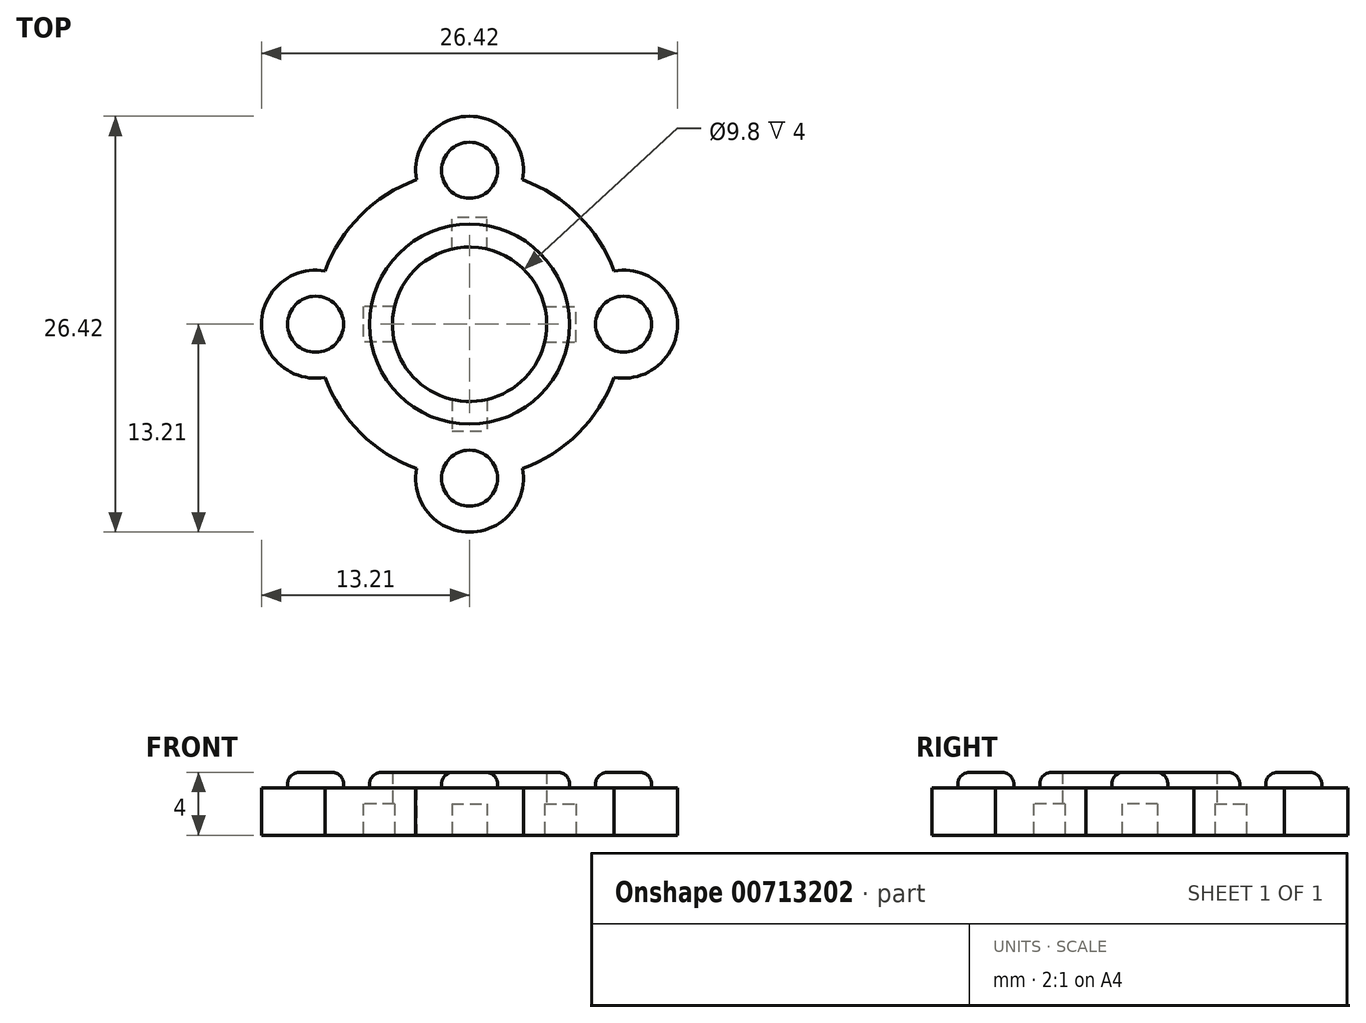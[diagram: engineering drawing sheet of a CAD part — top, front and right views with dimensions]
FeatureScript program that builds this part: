
annotation { "Feature Type Name" : "Feature", "Feature Type Description" : "" }
export const myFeature = defineFeature(function(context is Context, id is Id, definition is map)
    precondition{}
    {
        {
            var Q0;
            Q0=qCreatedBy(makeId("Top.planeOp"),FACE);
            var sketch = newSketch(context, id + "F0", { "sketchPlane" : qUnion([Q0])});
            skCircle(sketch, "E0", {"center": v(0, 0) * mm, "radius": 6.35 * mm});
            skCircle(sketch, "E1", {"center": v(0, 0) * mm, "radius": 9.78 * mm});
            skCircle(sketch, "E2", {"center": v(0, 9.78) * mm, "radius": 1.78 * mm});
            skCircle(sketch, "E3", {"center": v(0, 9.78) * mm, "radius": 3.43 * mm});
            skCircle(sketch, "E4.1.0", {"center": v(-9.78, 0) * mm, "radius": 3.43 * mm});
            skCircle(sketch, "E4.1.1", {"center": v(-9.78, 0) * mm, "radius": 1.78 * mm});
            skCircle(sketch, "E4.2.0", {"center": v(0, -9.78) * mm, "radius": 3.43 * mm});
            skCircle(sketch, "E4.2.1", {"center": v(0, -9.78) * mm, "radius": 1.78 * mm});
            skCircle(sketch, "E4.3.0", {"center": v(9.78, 0) * mm, "radius": 3.43 * mm});
            skCircle(sketch, "E4.3.1", {"center": v(9.78, 0) * mm, "radius": 1.78 * mm});
            skCircle(sketch, "E5", {"center": v(0, 0) * mm, "radius": 4.9 * mm});
            skSolve(sketch);
        }
        {
            var Q0;
            {var subQ0=sQuery(id+"F0.wireOp",EDGE,"E4.1.1");var subQ1=sQuery(id+"F0.wireOp",EDGE,"E1");var subQ2=makeQuery(id+"F0.imprint","INTERSECT",VERTEX,{"disambiguationData":[OD(0.0)],"derivedFrom":[subQ1,subQ0]});Q0=makeQuery(id+"F0.imprint","IMPRINT",FACE,{"disambiguationData":[TD([[makeQuery(id+"F0.imprint","IMPRINT",EDGE,{"disambiguationData":[TD([[subQ2,-1.0]])],"derivedFrom":subQ1}),-1.0]])]});}
            var Q1;
            {var subQ0=sQuery(id+"F0.wireOp",EDGE,"E2");var subQ1=sQuery(id+"F0.wireOp",EDGE,"E1");var subQ2=makeQuery(id+"F0.imprint","INTERSECT",VERTEX,{"disambiguationData":[OD(0.0)],"derivedFrom":[subQ1,subQ0]});Q1=makeQuery(id+"F0.imprint","IMPRINT",FACE,{"disambiguationData":[TD([[makeQuery(id+"F0.imprint","IMPRINT",EDGE,{"disambiguationData":[TD([[subQ2,-1.0]])],"derivedFrom":subQ1}),-1.0]])]});}
            var Q2;
            {var subQ0=sQuery(id+"F0.wireOp",EDGE,"E4.1.0");var subQ1=sQuery(id+"F0.wireOp",EDGE,"E0");var subQ2=makeQuery(id+"F0.imprint","INTERSECT",VERTEX,{"derivedFrom":[subQ1,subQ0]});Q2=makeQuery(id+"F0.imprint","IMPRINT",FACE,{"disambiguationData":[TD([[makeQuery(id+"F0.imprint","IMPRINT",EDGE,{"disambiguationData":[TD([[subQ2,-1.0]])],"derivedFrom":subQ1}),-1.0]])]});}
            var Q3;
            {var subQ0=sQuery(id+"F0.wireOp",EDGE,"E4.1.1");var subQ1=sQuery(id+"F0.wireOp",EDGE,"E1");var subQ2=makeQuery(id+"F0.imprint","INTERSECT",VERTEX,{"disambiguationData":[OD(0.0)],"derivedFrom":[subQ1,subQ0]});Q3=makeQuery(id+"F0.imprint","IMPRINT",FACE,{"disambiguationData":[TD([[makeQuery(id+"F0.imprint","IMPRINT",EDGE,{"disambiguationData":[TD([[subQ2,-1.0]])],"derivedFrom":subQ1}),1.0]])]});}
            var Q4;
            {var subQ0=sQuery(id+"F0.wireOp",EDGE,"E4.2.0");var subQ1=sQuery(id+"F0.wireOp",EDGE,"E1");var subQ4=makeQuery(id+"F0.imprint","INTERSECT",VERTEX,{"disambiguationData":[OD(0.0)],"derivedFrom":[subQ1,subQ0]});Q4=makeQuery(id+"F0.imprint","IMPRINT",FACE,{"disambiguationData":[TD([[makeQuery(id+"F0.imprint","IMPRINT",EDGE,{"disambiguationData":[TD([[subQ4,-1.0]])],"derivedFrom":subQ1}),1.0]])]});}
            var Q5;
            {var subQ0=sQuery(id+"F0.wireOp",EDGE,"E4.3.0");var subQ1=sQuery(id+"F0.wireOp",EDGE,"E1");var subQ4=makeQuery(id+"F0.imprint","INTERSECT",VERTEX,{"disambiguationData":[OD(0.0)],"derivedFrom":[subQ1,subQ0]});Q5=makeQuery(id+"F0.imprint","IMPRINT",FACE,{"disambiguationData":[TD([[makeQuery(id+"F0.imprint","IMPRINT",EDGE,{"disambiguationData":[TD([[subQ4,1.0]])],"derivedFrom":subQ1}),1.0]])]});}
            var Q6;
            {var subQ0=sQuery(id+"F0.wireOp",EDGE,"E4.1.0");var subQ1=sQuery(id+"F0.wireOp",EDGE,"E1");var subQ2=makeQuery(id+"F0.imprint","INTERSECT",VERTEX,{"disambiguationData":[OD(0.0)],"derivedFrom":[subQ1,subQ0]});Q6=makeQuery(id+"F0.imprint","IMPRINT",FACE,{"disambiguationData":[TD([[makeQuery(id+"F0.imprint","IMPRINT",EDGE,{"disambiguationData":[TD([[subQ2,-1.0]])],"derivedFrom":subQ1}),1.0]])]});}
            var Q7;
            {var subQ0=sQuery(id+"F0.wireOp",EDGE,"E4.3.1");var subQ1=sQuery(id+"F0.wireOp",EDGE,"E1");var subQ2=makeQuery(id+"F0.imprint","INTERSECT",VERTEX,{"disambiguationData":[OD(0.0)],"derivedFrom":[subQ1,subQ0]});Q7=makeQuery(id+"F0.imprint","IMPRINT",FACE,{"disambiguationData":[TD([[makeQuery(id+"F0.imprint","IMPRINT",EDGE,{"disambiguationData":[TD([[subQ2,1.0]])],"derivedFrom":subQ1}),-1.0]])]});}
            var Q8;
            {var subQ0=sQuery(id+"F0.wireOp",EDGE,"E4.2.1");var subQ1=sQuery(id+"F0.wireOp",EDGE,"E1");var subQ2=makeQuery(id+"F0.imprint","INTERSECT",VERTEX,{"disambiguationData":[OD(0.0)],"derivedFrom":[subQ1,subQ0]});Q8=makeQuery(id+"F0.imprint","IMPRINT",FACE,{"disambiguationData":[TD([[makeQuery(id+"F0.imprint","IMPRINT",EDGE,{"disambiguationData":[TD([[subQ2,-1.0]])],"derivedFrom":subQ1}),-1.0]])]});}
            var Q9;
            {var subQ0=sQuery(id+"F0.wireOp",EDGE,"E4.1.0");var subQ1=sQuery(id+"F0.wireOp",EDGE,"E1");var subQ2=makeQuery(id+"F0.imprint","INTERSECT",VERTEX,{"disambiguationData":[OD(0.0)],"derivedFrom":[subQ1,subQ0]});Q9=makeQuery(id+"F0.imprint","IMPRINT",FACE,{"disambiguationData":[TD([[makeQuery(id+"F0.imprint","IMPRINT",EDGE,{"disambiguationData":[TD([[subQ2,-1.0]])],"derivedFrom":subQ1}),-1.0]])]});}
            var Q10;
            {var subQ0=sQuery(id+"F0.wireOp",EDGE,"E2");var subQ1=sQuery(id+"F0.wireOp",EDGE,"E1");var subQ2=makeQuery(id+"F0.imprint","INTERSECT",VERTEX,{"disambiguationData":[OD(0.0)],"derivedFrom":[subQ1,subQ0]});Q10=makeQuery(id+"F0.imprint","IMPRINT",FACE,{"disambiguationData":[TD([[makeQuery(id+"F0.imprint","IMPRINT",EDGE,{"disambiguationData":[TD([[subQ2,-1.0]])],"derivedFrom":subQ1}),1.0]])]});}
            var Q11;
            {var subQ0=sQuery(id+"F0.wireOp",EDGE,"E3");var subQ1=sQuery(id+"F0.wireOp",EDGE,"E1");var subQ2=makeQuery(id+"F0.imprint","INTERSECT",VERTEX,{"disambiguationData":[OD(0.0)],"derivedFrom":[subQ1,subQ0]});Q11=makeQuery(id+"F0.imprint","IMPRINT",FACE,{"disambiguationData":[TD([[makeQuery(id+"F0.imprint","IMPRINT",EDGE,{"disambiguationData":[TD([[subQ2,-1.0]])],"derivedFrom":subQ1}),-1.0]])]});}
            var Q12;
            {var subQ0=sQuery(id+"F0.wireOp",EDGE,"E4.3.0");var subQ1=sQuery(id+"F0.wireOp",EDGE,"E1");var subQ2=makeQuery(id+"F0.imprint","INTERSECT",VERTEX,{"disambiguationData":[OD(0.0)],"derivedFrom":[subQ1,subQ0]});Q12=makeQuery(id+"F0.imprint","IMPRINT",FACE,{"disambiguationData":[TD([[makeQuery(id+"F0.imprint","IMPRINT",EDGE,{"disambiguationData":[TD([[subQ2,1.0]])],"derivedFrom":subQ1}),-1.0]])]});}
            var Q13;
            Q13=makeQuery(id+"F0.imprint","IMPRINT",FACE,{"disambiguationData":[TD([[makeQuery(id+"F0.imprint","IMPRINT",EDGE,{"derivedFrom":sQuery(id+"F0.wireOp",EDGE,"E5")}),-1.0]])]});
            var Q14;
            {var subQ0=sQuery(id+"F0.wireOp",EDGE,"E3");var subQ1=sQuery(id+"F0.wireOp",EDGE,"E0");var subQ2=makeQuery(id+"F0.imprint","INTERSECT",VERTEX,{"derivedFrom":[subQ1,subQ0]});Q14=makeQuery(id+"F0.imprint","IMPRINT",FACE,{"disambiguationData":[TD([[makeQuery(id+"F0.imprint","IMPRINT",EDGE,{"disambiguationData":[TD([[subQ2,-1.0]])],"derivedFrom":subQ1}),-1.0]])]});}
            var Q15;
            {var subQ0=sQuery(id+"F0.wireOp",EDGE,"E4.3.0");var subQ1=sQuery(id+"F0.wireOp",EDGE,"E0");var subQ2=makeQuery(id+"F0.imprint","INTERSECT",VERTEX,{"derivedFrom":[subQ1,subQ0]});Q15=makeQuery(id+"F0.imprint","IMPRINT",FACE,{"disambiguationData":[TD([[makeQuery(id+"F0.imprint","IMPRINT",EDGE,{"disambiguationData":[TD([[subQ2,1.0]])],"derivedFrom":subQ1}),-1.0]])]});}
            var Q16;
            {var subQ0=sQuery(id+"F0.wireOp",EDGE,"E3");var subQ1=sQuery(id+"F0.wireOp",EDGE,"E0");var subQ2=makeQuery(id+"F0.imprint","INTERSECT",VERTEX,{"derivedFrom":[subQ1,subQ0]});Q16=makeQuery(id+"F0.imprint","IMPRINT",FACE,{"disambiguationData":[TD([[makeQuery(id+"F0.imprint","IMPRINT",EDGE,{"disambiguationData":[TD([[subQ2,1.0]])],"derivedFrom":subQ1}),-1.0]])]});}
            var Q17;
            {var subQ0=sQuery(id+"F0.wireOp",EDGE,"E4.3.1");var subQ1=sQuery(id+"F0.wireOp",EDGE,"E1");var subQ2=makeQuery(id+"F0.imprint","INTERSECT",VERTEX,{"disambiguationData":[OD(0.0)],"derivedFrom":[subQ1,subQ0]});Q17=makeQuery(id+"F0.imprint","IMPRINT",FACE,{"disambiguationData":[TD([[makeQuery(id+"F0.imprint","IMPRINT",EDGE,{"disambiguationData":[TD([[subQ2,1.0]])],"derivedFrom":subQ1}),1.0]])]});}
            var Q18;
            {var subQ0=sQuery(id+"F0.wireOp",EDGE,"E4.2.1");var subQ1=sQuery(id+"F0.wireOp",EDGE,"E1");var subQ2=makeQuery(id+"F0.imprint","INTERSECT",VERTEX,{"disambiguationData":[OD(0.0)],"derivedFrom":[subQ1,subQ0]});Q18=makeQuery(id+"F0.imprint","IMPRINT",FACE,{"disambiguationData":[TD([[makeQuery(id+"F0.imprint","IMPRINT",EDGE,{"disambiguationData":[TD([[subQ2,-1.0]])],"derivedFrom":subQ1}),1.0]])]});}
            var Q19;
            {var subQ0=sQuery(id+"F0.wireOp",EDGE,"E3");var subQ1=sQuery(id+"F0.wireOp",EDGE,"E1");var subQ7=makeQuery(id+"F0.imprint","INTERSECT",VERTEX,{"disambiguationData":[OD(0.0)],"derivedFrom":[subQ1,subQ0]});Q19=makeQuery(id+"F0.imprint","IMPRINT",FACE,{"disambiguationData":[TD([[makeQuery(id+"F0.imprint","IMPRINT",EDGE,{"disambiguationData":[TD([[subQ7,-1.0]])],"derivedFrom":subQ1}),1.0]])]});}
            var Q20;
            {var subQ0=sQuery(id+"F0.wireOp",EDGE,"E4.2.0");var subQ1=sQuery(id+"F0.wireOp",EDGE,"E1");var subQ2=makeQuery(id+"F0.imprint","INTERSECT",VERTEX,{"disambiguationData":[OD(0.0)],"derivedFrom":[subQ1,subQ0]});Q20=makeQuery(id+"F0.imprint","IMPRINT",FACE,{"disambiguationData":[TD([[makeQuery(id+"F0.imprint","IMPRINT",EDGE,{"disambiguationData":[TD([[subQ2,-1.0]])],"derivedFrom":subQ1}),-1.0]])]});}
            extrude(context, id + "F1", {"entities" : qUnion([Q0, Q1, Q2, Q3, Q4, Q5, Q6, Q7, Q8, Q9, Q10, Q11, Q12, Q13, Q14, Q15, Q16, Q17, Q18, Q19, Q20]), "depth" : 3 * mm, "offsetDistance" : 25 * mm});
        }
        {
            var Q0;
            Q0=makeQuery(id+"F0.imprint","IMPRINT",FACE,{"disambiguationData":[TD([[makeQuery(id+"F0.imprint","IMPRINT",EDGE,{"derivedFrom":sQuery(id+"F0.wireOp",EDGE,"E5")}),-1.0]])]});
            var Q1;
            {var subQ0=sQuery(id+"F0.wireOp",EDGE,"E4.1.1");var subQ1=sQuery(id+"F0.wireOp",EDGE,"E1");var subQ2=makeQuery(id+"F0.imprint","INTERSECT",VERTEX,{"disambiguationData":[OD(0.0)],"derivedFrom":[subQ1,subQ0]});Q1=makeQuery(id+"F0.imprint","IMPRINT",FACE,{"disambiguationData":[TD([[makeQuery(id+"F0.imprint","IMPRINT",EDGE,{"disambiguationData":[TD([[subQ2,-1.0]])],"derivedFrom":subQ1}),-1.0]])]});}
            var Q2;
            {var subQ0=sQuery(id+"F0.wireOp",EDGE,"E4.1.1");var subQ1=sQuery(id+"F0.wireOp",EDGE,"E1");var subQ2=makeQuery(id+"F0.imprint","INTERSECT",VERTEX,{"disambiguationData":[OD(0.0)],"derivedFrom":[subQ1,subQ0]});Q2=makeQuery(id+"F0.imprint","IMPRINT",FACE,{"disambiguationData":[TD([[makeQuery(id+"F0.imprint","IMPRINT",EDGE,{"disambiguationData":[TD([[subQ2,-1.0]])],"derivedFrom":subQ1}),1.0]])]});}
            var Q3;
            {var subQ0=sQuery(id+"F0.wireOp",EDGE,"E2");var subQ1=sQuery(id+"F0.wireOp",EDGE,"E1");var subQ2=makeQuery(id+"F0.imprint","INTERSECT",VERTEX,{"disambiguationData":[OD(0.0)],"derivedFrom":[subQ1,subQ0]});Q3=makeQuery(id+"F0.imprint","IMPRINT",FACE,{"disambiguationData":[TD([[makeQuery(id+"F0.imprint","IMPRINT",EDGE,{"disambiguationData":[TD([[subQ2,-1.0]])],"derivedFrom":subQ1}),-1.0]])]});}
            var Q4;
            {var subQ0=sQuery(id+"F0.wireOp",EDGE,"E2");var subQ1=sQuery(id+"F0.wireOp",EDGE,"E1");var subQ2=makeQuery(id+"F0.imprint","INTERSECT",VERTEX,{"disambiguationData":[OD(0.0)],"derivedFrom":[subQ1,subQ0]});Q4=makeQuery(id+"F0.imprint","IMPRINT",FACE,{"disambiguationData":[TD([[makeQuery(id+"F0.imprint","IMPRINT",EDGE,{"disambiguationData":[TD([[subQ2,-1.0]])],"derivedFrom":subQ1}),1.0]])]});}
            var Q5;
            {var subQ0=sQuery(id+"F0.wireOp",EDGE,"E4.3.1");var subQ1=sQuery(id+"F0.wireOp",EDGE,"E1");var subQ2=makeQuery(id+"F0.imprint","INTERSECT",VERTEX,{"disambiguationData":[OD(0.0)],"derivedFrom":[subQ1,subQ0]});Q5=makeQuery(id+"F0.imprint","IMPRINT",FACE,{"disambiguationData":[TD([[makeQuery(id+"F0.imprint","IMPRINT",EDGE,{"disambiguationData":[TD([[subQ2,1.0]])],"derivedFrom":subQ1}),-1.0]])]});}
            var Q6;
            {var subQ0=sQuery(id+"F0.wireOp",EDGE,"E4.3.1");var subQ1=sQuery(id+"F0.wireOp",EDGE,"E1");var subQ2=makeQuery(id+"F0.imprint","INTERSECT",VERTEX,{"disambiguationData":[OD(0.0)],"derivedFrom":[subQ1,subQ0]});Q6=makeQuery(id+"F0.imprint","IMPRINT",FACE,{"disambiguationData":[TD([[makeQuery(id+"F0.imprint","IMPRINT",EDGE,{"disambiguationData":[TD([[subQ2,1.0]])],"derivedFrom":subQ1}),1.0]])]});}
            var Q7;
            {var subQ0=sQuery(id+"F0.wireOp",EDGE,"E4.2.1");var subQ1=sQuery(id+"F0.wireOp",EDGE,"E1");var subQ2=makeQuery(id+"F0.imprint","INTERSECT",VERTEX,{"disambiguationData":[OD(0.0)],"derivedFrom":[subQ1,subQ0]});Q7=makeQuery(id+"F0.imprint","IMPRINT",FACE,{"disambiguationData":[TD([[makeQuery(id+"F0.imprint","IMPRINT",EDGE,{"disambiguationData":[TD([[subQ2,-1.0]])],"derivedFrom":subQ1}),1.0]])]});}
            var Q8;
            {var subQ0=sQuery(id+"F0.wireOp",EDGE,"E4.2.1");var subQ1=sQuery(id+"F0.wireOp",EDGE,"E1");var subQ2=makeQuery(id+"F0.imprint","INTERSECT",VERTEX,{"disambiguationData":[OD(0.0)],"derivedFrom":[subQ1,subQ0]});Q8=makeQuery(id+"F0.imprint","IMPRINT",FACE,{"disambiguationData":[TD([[makeQuery(id+"F0.imprint","IMPRINT",EDGE,{"disambiguationData":[TD([[subQ2,-1.0]])],"derivedFrom":subQ1}),-1.0]])]});}
            extrude(context, id + "F2", {"entities" : qUnion([Q0, Q1, Q2, Q3, Q4, Q5, Q6, Q7, Q8]), "operationType" : NewBodyOperationType.ADD, "depth" : 4 * mm, "offsetDistance" : 25 * mm});
        }
        {
            var Q0;
            Q0=makeQuery(id+"F0.imprint","IMPRINT",FACE,{"disambiguationData":[TD([[makeQuery(id+"F0.imprint","IMPRINT",EDGE,{"derivedFrom":sQuery(id+"F0.wireOp",EDGE,"E5")}),1.0]])]});
            var sketch = newSketch(context, id + "F3", { "sketchPlane" : qUnion([Q0])});
            skLineSegment(sketch, "E6.bottom", {"start": v(1.13, 4.77) * mm, "end": v(-1.13, 4.77) * mm});
            skLineSegment(sketch, "E6.top", {"start": v(1.12, 6.77) * mm, "end": v(-1.12, 6.77) * mm});
            skLineSegment(sketch, "E6.left", {"start": v(1.13, 4.77) * mm, "end": v(1.13, 6.77) * mm});
            skLineSegment(sketch, "E6.right", {"start": v(-1.13, 4.77) * mm, "end": v(-1.13, 6.77) * mm});
            skPoint(sketch, "E6.middle", {"position": v(0, 5.77) * mm});
            skLineSegment(sketch, "E7.1.0", {"start": v(-4.77, -1.13) * mm, "end": v(-6.77, -1.13) * mm});
            skLineSegment(sketch, "E7.1.1", {"start": v(-4.77, 1.13) * mm, "end": v(-6.77, 1.13) * mm});
            skLineSegment(sketch, "E7.1.2", {"start": v(-6.77, 1.13) * mm, "end": v(-6.77, -1.13) * mm});
            skLineSegment(sketch, "E7.1.3", {"start": v(-4.77, 1.13) * mm, "end": v(-4.77, -1.13) * mm});
            skLineSegment(sketch, "E7.2.0", {"start": v(1.12, -4.77) * mm, "end": v(1.12, -6.77) * mm});
            skLineSegment(sketch, "E7.2.1", {"start": v(-1.13, -4.77) * mm, "end": v(-1.13, -6.77) * mm});
            skLineSegment(sketch, "E7.2.2", {"start": v(-1.13, -6.77) * mm, "end": v(1.12, -6.77) * mm});
            skLineSegment(sketch, "E7.2.3", {"start": v(-1.13, -4.77) * mm, "end": v(1.13, -4.77) * mm});
            skLineSegment(sketch, "E7.3.0", {"start": v(4.77, 1.13) * mm, "end": v(6.77, 1.13) * mm});
            skLineSegment(sketch, "E7.3.1", {"start": v(4.77, -1.13) * mm, "end": v(6.77, -1.13) * mm});
            skLineSegment(sketch, "E7.3.2", {"start": v(6.77, -1.12) * mm, "end": v(6.77, 1.12) * mm});
            skLineSegment(sketch, "E7.3.3", {"start": v(4.77, -1.13) * mm, "end": v(4.77, 1.13) * mm});
            skPoint(sketch, "E7.center", {"position": v(0, 0) * mm});
            skCircle(sketch, "E8.0", {"center": v(0, 0) * mm, "radius": 4.9 * mm});
            skSolve(sketch);
        }
        {
            var Q0;
            Q0=makeQuery(id+"F3.imprint","IMPRINT",FACE,{"disambiguationData":[TD([[makeQuery(id+"F3.imprint","IMPRINT",EDGE,{"derivedFrom":sQuery(id+"F3.wireOp",EDGE,"E6.top")}),1.0]])]});
            var Q1;
            {var subQ0=sQuery(id+"F3.wireOp",EDGE,"E7.3.0");Q1=makeQuery(id+"F3.imprint","IMPRINT",FACE,{"disambiguationData":[TD([[makeQuery(id+"F3.imprint","IMPRINT",EDGE,{"derivedFrom":subQ0}),-1.0]])]});}
            var Q2;
            {var subQ0=sQuery(id+"F3.wireOp",EDGE,"E7.2.0");Q2=makeQuery(id+"F3.imprint","IMPRINT",FACE,{"disambiguationData":[TD([[makeQuery(id+"F3.imprint","IMPRINT",EDGE,{"derivedFrom":subQ0}),-1.0]])]});}
            var Q3;
            {var subQ0=sQuery(id+"F3.wireOp",EDGE,"E7.1.0");Q3=makeQuery(id+"F3.imprint","IMPRINT",FACE,{"disambiguationData":[TD([[makeQuery(id+"F3.imprint","IMPRINT",EDGE,{"derivedFrom":subQ0}),-1.0]])]});}
            extrude(context, id + "F4", {"entities" : qUnion([Q0, Q1, Q2, Q3]), "operationType" : NewBodyOperationType.REMOVE, "depth" : 2 * mm, "offsetDistance" : 25 * mm});
        }
        {
            var Q0;
            Q0=makeQuery(id+"F2.opExtrude","CAP_EDGE",EDGE,{"disambiguationData":[OSD([sQuery(id+"F0.wireOp",EDGE,"E4.1.1")])],"isStart":false});
            var Q1;
            Q1=makeQuery(id+"F2.opExtrude","CAP_EDGE",EDGE,{"disambiguationData":[OSD([sQuery(id+"F0.wireOp",EDGE,"E2")])],"isStart":false});
            var Q2;
            Q2=makeQuery(id+"F2.opExtrude","CAP_EDGE",EDGE,{"disambiguationData":[OSD([sQuery(id+"F0.wireOp",EDGE,"E4.3.1")])],"isStart":false});
            var Q3;
            Q3=makeQuery(id+"F2.opExtrude","CAP_EDGE",EDGE,{"disambiguationData":[OSD([sQuery(id+"F0.wireOp",EDGE,"E4.2.1")])],"isStart":false});
            var Q4;
            Q4=makeQuery(id+"F2.opExtrude","CAP_EDGE",EDGE,{"disambiguationData":[OSD([sQuery(id+"F0.wireOp",EDGE,"E0")])],"isStart":false});
            fillet(context, id + "F5", {"entities" : qUnion([Q0, Q1, Q2, Q3, Q4]), "radius" : .75 * mm, "tangentPropagation" : true, "allowEdgeOverflow" : false});
        }
    });
